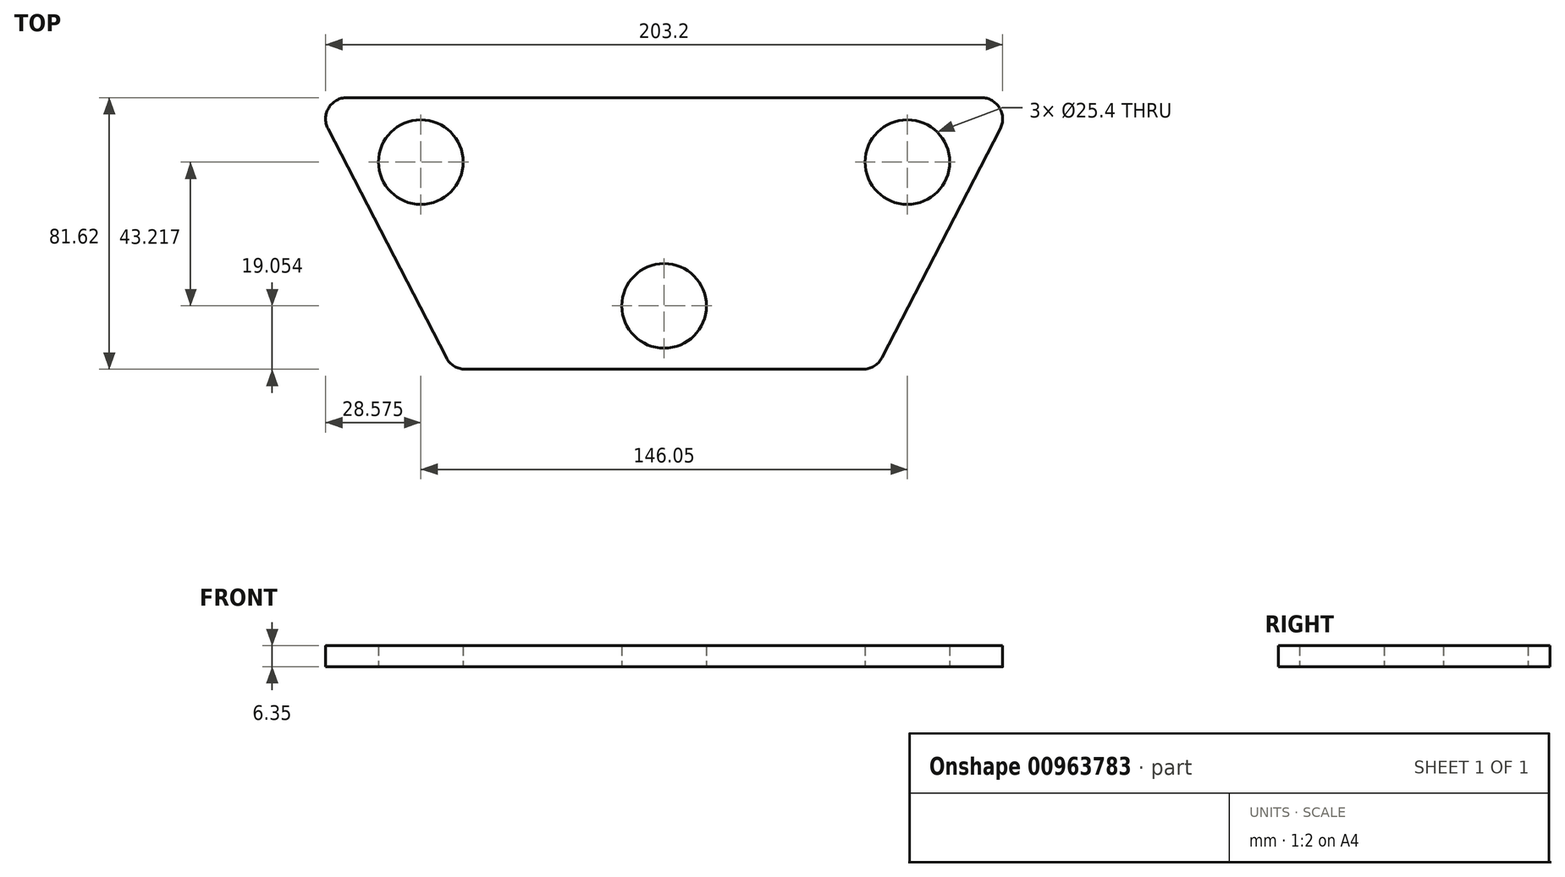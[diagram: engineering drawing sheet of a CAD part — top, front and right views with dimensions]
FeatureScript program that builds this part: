
annotation { "Feature Type Name" : "Feature", "Feature Type Description" : "" }
export const myFeature = defineFeature(function(context is Context, id is Id, definition is map)
    precondition{}
    {
        {
            var Q0;
            Q0=qCreatedBy(makeId("Top.planeOp"),FACE);
            var sketch = newSketch(context, id + "F0", { "sketchPlane" : qUnion([Q0])});
            skLineSegment(sketch, "E0", {"start": v(0, 41.33) * mm, "end": v(0, -8.54) * mm});
            skLineSegment(sketch, "E1", {"start": v(0, -40.29) * mm, "end": v(59.7, -40.29) * mm});
            skLineSegment(sketch, "E2", {"start": v(65.34, -36.85) * mm, "end": v(100.9, 32.06) * mm});
            skLineSegment(sketch, "E3", {"start": v(95.25, 41.33) * mm, "end": v(0, 41.33) * mm});
            skCircle(sketch, "E4", {"center": v(73.02, 21.98) * mm, "radius": 12.7 * mm});
            skArc(sketch, "E5", {"start": v(0, -33.94) * mm, "mid": v(12.7, -21.24) * mm, "end": v(0, -8.54) * mm});
            skArc(sketch, "E6.MirrorCS", {"start": v(0, -33.94) * mm, "mid": v(-12.7, -21.24) * mm, "end": v(0, -8.54) * mm});
            skLineSegment(sketch, "E7.MirrorCS", {"start": v(0, -40.29) * mm, "end": v(-59.7, -40.29) * mm});
            skLineSegment(sketch, "E8.MirrorCS", {"start": v(-65.34, -36.85) * mm, "end": v(-100.9, 32.06) * mm});
            skCircle(sketch, "E9.MirrorC", {"center": v(-73.02, 21.98) * mm, "radius": 12.7 * mm});
            skLineSegment(sketch, "E10.MirrorCS", {"start": v(-95.25, 41.33) * mm, "end": v(0, 41.33) * mm});
            skLineSegment(sketch, "E11.trimOffspring", {"start": v(0, -33.94) * mm, "end": v(0, -40.29) * mm});
            skPoint(sketch, "E12.visualSharp", {"position": v(-105.67, 41.33) * mm});
            skArc(sketch, "E12.filletArc", {"start": v(-95.25, 41.33) * mm, "mid": v(-100.67, 38.28) * mm, "end": v(-100.9, 32.06) * mm});
            skPoint(sketch, "E13.visualSharp", {"position": v(105.67, 41.33) * mm});
            skArc(sketch, "E13.filletArc", {"start": v(100.9, 32.06) * mm, "mid": v(100.67, 38.28) * mm, "end": v(95.25, 41.33) * mm});
            skPoint(sketch, "E14.visualSharp", {"position": v(63.57, -40.29) * mm});
            skArc(sketch, "E14.filletArc", {"start": v(59.7, -40.29) * mm, "mid": v(63, -39.36) * mm, "end": v(65.34, -36.85) * mm});
            skPoint(sketch, "E15.visualSharp", {"position": v(-63.57, -40.29) * mm});
            skArc(sketch, "E15.filletArc", {"start": v(-65.34, -36.85) * mm, "mid": v(-63, -39.36) * mm, "end": v(-59.7, -40.29) * mm});
            skSolve(sketch);
        }
        {
            var Q0;
            Q0=makeQuery(id+"F0.imprint","IMPRINT",FACE,{"disambiguationData":[TD([[makeQuery(id+"F0.imprint","IMPRINT",EDGE,{"derivedFrom":sQuery(id+"F0.wireOp",EDGE,"E0")}),-1.0]])]});
            var Q1;
            Q1=makeQuery(id+"F0.imprint","IMPRINT",FACE,{"disambiguationData":[TD([[makeQuery(id+"F0.imprint","IMPRINT",EDGE,{"derivedFrom":sQuery(id+"F0.wireOp",EDGE,"E0")}),1.0]])]});
            extrude(context, id + "F1", {"entities" : qUnion([Q0, Q1]), "depth" : 6.35 * mm, "offsetDistance" : 25.4 * mm});
        }
    });
